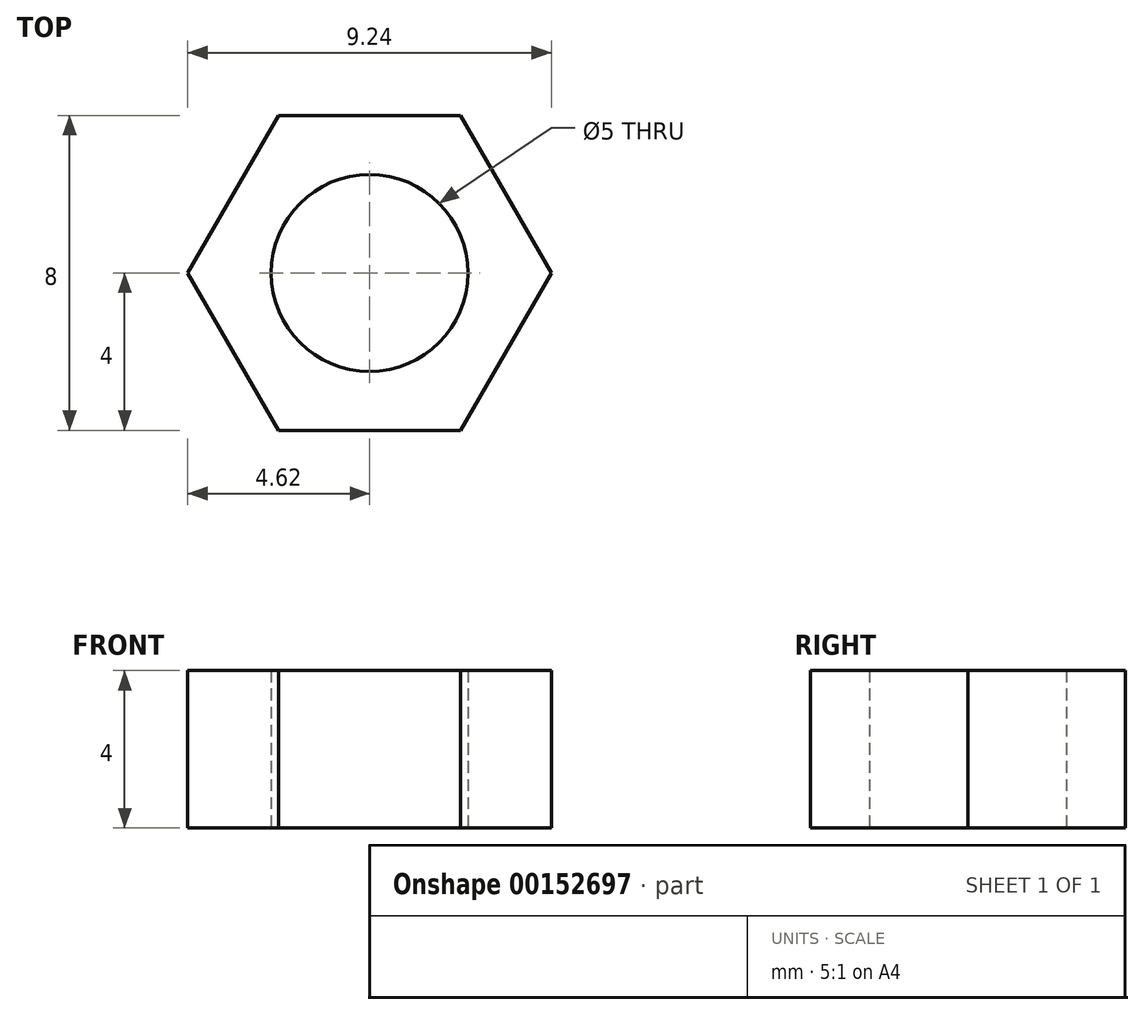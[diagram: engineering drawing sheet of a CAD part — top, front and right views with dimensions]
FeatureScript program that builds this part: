
annotation { "Feature Type Name" : "Feature", "Feature Type Description" : "" }
export const myFeature = defineFeature(function(context is Context, id is Id, definition is map)
    precondition{}
    {
        {
            var Q0;
            Q0=qCreatedBy(makeId("Top.planeOp"),FACE);
            var sketch = newSketch(context, id + "F0", { "sketchPlane" : qUnion([Q0])});
            skCircle(sketch, "E0.cCircle", {"center": v(0, 0) * mm, "radius": 4 * mm, "construction": true});
            skLineSegment(sketch, "E0.0", {"start": v(2.3, -4) * mm, "end": v(-2.3, -4) * mm});
            skLineSegment(sketch, "E0.1", {"start": v(-2.3, -4) * mm, "end": v(-4.62, 0) * mm});
            skLineSegment(sketch, "E0.2", {"start": v(-4.62, 0) * mm, "end": v(-2.3, 4) * mm});
            skLineSegment(sketch, "E0.3", {"start": v(-2.3, 4) * mm, "end": v(2.3, 4) * mm});
            skLineSegment(sketch, "E0.4", {"start": v(2.3, 4) * mm, "end": v(4.62, 0) * mm});
            skLineSegment(sketch, "E0.5", {"start": v(4.62, 0) * mm, "end": v(2.3, -4) * mm});
            skPoint(sketch, "E0.0.midPoint", {"position": v(0, -4) * mm});
            skCircle(sketch, "E1", {"center": v(0, 0) * mm, "radius": 2.5 * mm});
            skSolve(sketch);
        }
        {
            var Q0;
            Q0 = qSketchRegion(id + "F0", true);
            extrude(context, id + "F1", {"entities" : qUnion([Q0]), "depth" : 4 * mm});
        }
    });
